# Revit family: Accessory-Tissue_Holder-KOHLER-July-K-29229T-1
name_source: partatom
category: Specialty Equipment
units: mm (PartAtom-declared; Revit-internal decimal feet)

## family parameters
Cut with Voids When Loaded = No
Enable Cutting in Views = No
Host = Face
Maintain Annotation Orientation = No
OmniClass Number = 23.31.25.21
Part Type = Normal
Room Calculation Point = No
Round Connector Dimension = Use Diameter
Shared = No

## types (4) — shared parameters
ADA Compliant = No
Assembly Code = C1030200
Date Modified = 03/10/2026
Default Elevation = 42 in
Description = Double-layer toilet paper holder (with storage platform)
Height = 3 1/4 in
Length = 12 5/8 in
Manufacturer = Kohler Co.
Master Format 2014 = 10 28 00
Master Format 2014 Name = Toilet, Bath, and Laundry Accessories
Material = Premium Metal Construction
Product Documentation Link = https://files.kohler.com.cn
Product Name = July
Product Page URL = https://www.kohler.com.cn
URL = http://www.kohler.com.cn
WaterSense Certified = No
Width = 4 3/4 in

## per-type parameters (varying)
| type | Finish | Model | Type |
| BL-Matte Black | Kohler-Metal-BL-Matte_Black | K-29229T-BL | 1 |
| CP-Polished Chrome | Kohler-Metal-CP-Polished_Chrome | K-29229T-CP | 2 |
| DUN-Organic | KOHLER-Metal-DUN-Organic | K-29229T-DUN | 3 |
| LBN-Non Pvd Brushed Nickel | Kohler-Metal-LBN-Non_Pvd_Brushed_Nickel | K-29229T-LBN | 4 |

## geometry (parser evidence)
native form markers: Sweep x6
no freeform markers — native parametric forms only
